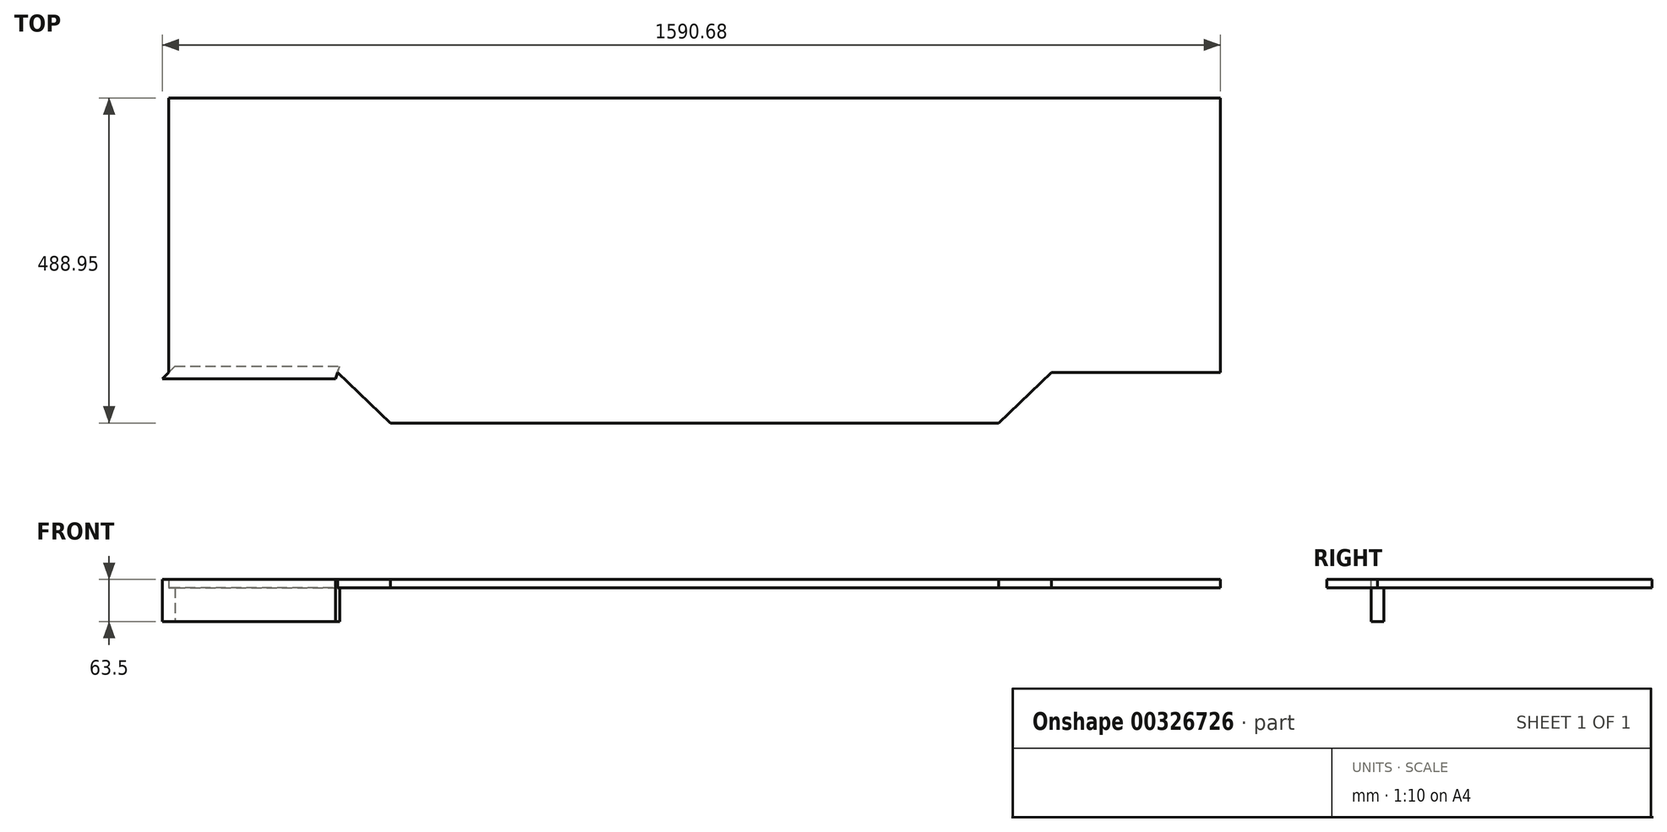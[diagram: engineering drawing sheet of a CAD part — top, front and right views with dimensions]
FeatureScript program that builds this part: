
annotation { "Feature Type Name" : "Feature", "Feature Type Description" : "" }
export const myFeature = defineFeature(function(context is Context, id is Id, definition is map)
    precondition{}
    {
        {
            var Q0;
            Q0=qCreatedBy(makeId("Top.planeOp"),FACE);
            var sketch = newSketch(context, id + "F0", { "sketchPlane" : qUnion([Q0])});
            skLineSegment(sketch, "E0", {"start": v(-790.58, 0) * mm, "end": v(-790.58, -412.75) * mm});
            skLineSegment(sketch, "E1", {"start": v(-790.58, -412.75) * mm, "end": v(-536.57, -412.75) * mm});
            skLineSegment(sketch, "E2", {"start": v(-536.57, -412.75) * mm, "end": v(-457.2, -488.95) * mm});
            skLineSegment(sketch, "E3", {"start": v(-457.2, -488.95) * mm, "end": v(457.2, -488.95) * mm});
            skLineSegment(sketch, "E4", {"start": v(457.2, -488.95) * mm, "end": v(536.57, -412.75) * mm});
            skLineSegment(sketch, "E5", {"start": v(536.57, -412.75) * mm, "end": v(790.58, -412.75) * mm});
            skLineSegment(sketch, "E6", {"start": v(790.58, -412.75) * mm, "end": v(790.58, 0) * mm});
            skLineSegment(sketch, "E7", {"start": v(790.58, 0) * mm, "end": v(-790.58, 0) * mm});
            skSolve(sketch);
        }
        {
            var Q0;
            Q0=makeQuery(id+"F0.imprint","IMPRINT",FACE,{"disambiguationData":[TD([[makeQuery(id+"F0.imprint","IMPRINT",EDGE,{"derivedFrom":sQuery(id+"F0.wireOp",EDGE,"E0")}),1.0]])]});
            extrude(context, id + "F1", {"entities" : qUnion([Q0]), "depth" : 12.7 * mm});
        }
        {
            var Q0;
            Q0=makeQuery(id+"F1.opExtrude","CAP_FACE",FACE,{"disambiguationData":[OSD([sQuery(id+"F0.wireOp",EDGE,"E0"),sQuery(id+"F0.wireOp",EDGE,"E1"),sQuery(id+"F0.wireOp",EDGE,"E2"),sQuery(id+"F0.wireOp",EDGE,"E3"),sQuery(id+"F0.wireOp",EDGE,"E4"),sQuery(id+"F0.wireOp",EDGE,"E5"),sQuery(id+"F0.wireOp",EDGE,"E6"),sQuery(id+"F0.wireOp",EDGE,"E7")])],"isStart":true});
            var sketch = newSketch(context, id + "F2", { "sketchPlane" : qUnion([Q0])});
            skLineSegment(sketch, "E8", {"start": v(-790.58, 412.75) * mm, "end": v(-800.1, 422.28) * mm});
            skLineSegment(sketch, "E9", {"start": v(-800.1, 422.28) * mm, "end": v(-539.67, 422.28) * mm});
            skLineSegment(sketch, "E10", {"start": v(-539.67, 422.28) * mm, "end": v(-536.57, 412.75) * mm});
            skLineSegment(sketch, "E11", {"start": v(-536.57, 412.75) * mm, "end": v(-790.58, 412.75) * mm});
            skSolve(sketch);
        }
        {
            var Q0;
            Q0=makeQuery(id+"F2.imprint","IMPRINT",FACE,{"disambiguationData":[TD([[makeQuery(id+"F2.imprint","IMPRINT",EDGE,{"derivedFrom":sQuery(id+"F2.wireOp",EDGE,"E8")}),-1.0]])]});
            extrude(context, id + "F3", {"entities" : qUnion([Q0]), "depth" : 50.8 * mm, "hasSecondDirection" : true, "secondDirectionOppositeDirection" : true, "secondDirectionDepth" : 12.7 * mm});
        }
        {
            var Q0;
            Q0=makeQuery(id+"F3.opExtrude","CAP_FACE",FACE,{"disambiguationData":[OSD([sQuery(id+"F2.wireOp",EDGE,"E8"),sQuery(id+"F2.wireOp",EDGE,"E9"),sQuery(id+"F2.wireOp",EDGE,"E10"),sQuery(id+"F2.wireOp",EDGE,"E11")])],"isStart":false});
            var sketch = newSketch(context, id + "F4", { "sketchPlane" : qUnion([Q0])});
            skLineSegment(sketch, "E12", {"start": v(-790.58, 412.75) * mm, "end": v(-781.05, 403.23) * mm});
            skLineSegment(sketch, "E13", {"start": v(-781.05, 403.23) * mm, "end": v(-533.48, 403.23) * mm});
            skLineSegment(sketch, "E14", {"start": v(-536.57, 412.75) * mm, "end": v(-533.48, 403.23) * mm});
            skSolve(sketch);
        }
        {
            var Q0;
            Q0=makeQuery(id+"F4.imprint","IMPRINT",FACE,{"disambiguationData":[TD([[makeQuery(id+"F4.imprint","IMPRINT",EDGE,{"derivedFrom":sQuery(id+"F4.wireOp",EDGE,"E12")}),1.0]])]});
            extrude(context, id + "F5", {"entities" : qUnion([Q0]), "operationType" : NewBodyOperationType.ADD, "oppositeDirection" : true, "depth" : 50.8 * mm});
        }
    });
